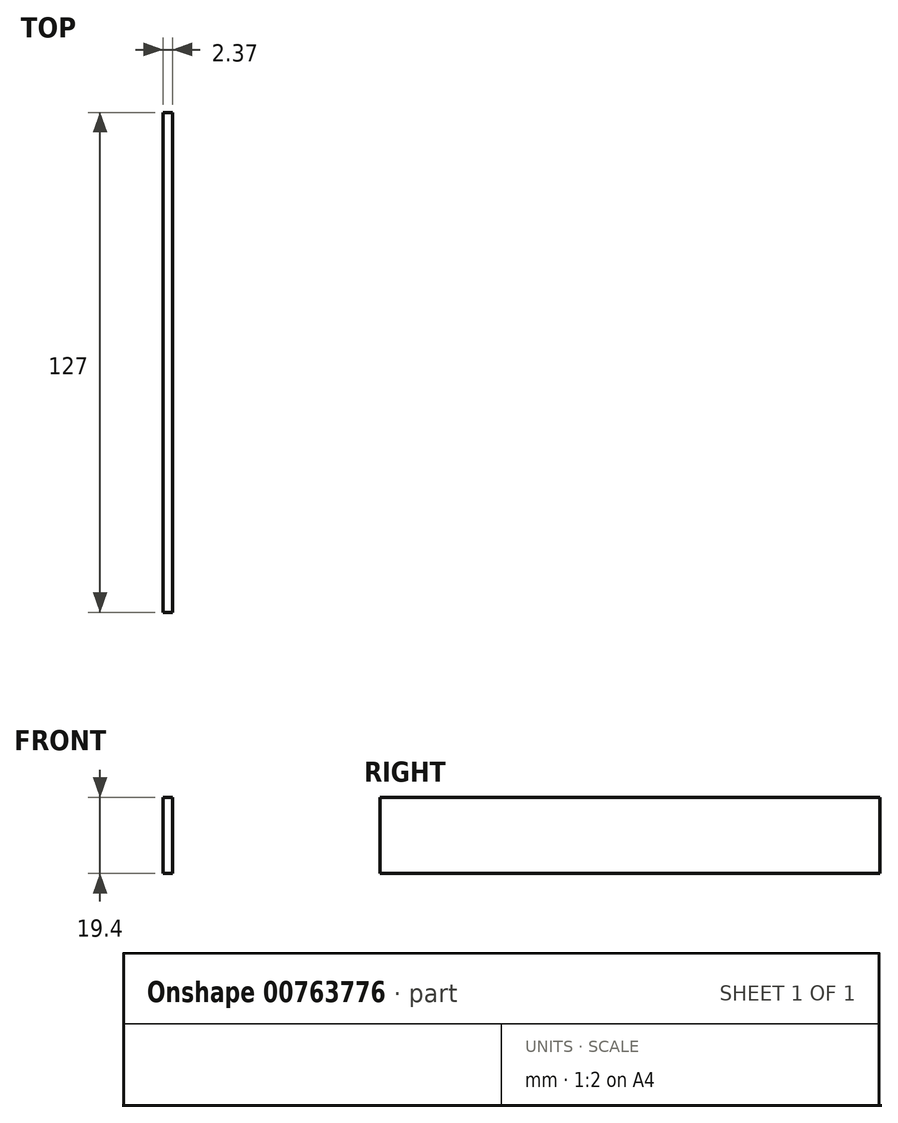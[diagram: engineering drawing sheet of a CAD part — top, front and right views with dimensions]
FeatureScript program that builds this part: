
annotation { "Feature Type Name" : "Feature", "Feature Type Description" : "" }
export const myFeature = defineFeature(function(context is Context, id is Id, definition is map)
    precondition{}
    {
        {
            var Q0;
            Q0=qCreatedBy(makeId("Front.planeOp"),FACE);
            var sketch = newSketch(context, id + "F0", { "sketchPlane" : qUnion([Q0])});
            skLineSegment(sketch, "E0.bottom", {"start": v(-47.21, 76.4) * mm, "end": v(-49.58, 76.4) * mm});
            skLineSegment(sketch, "E0.top", {"start": v(-47.21, 57) * mm, "end": v(-49.58, 57) * mm});
            skLineSegment(sketch, "E0.left", {"start": v(-47.21, 76.4) * mm, "end": v(-47.21, 57) * mm});
            skLineSegment(sketch, "E0.right", {"start": v(-49.58, 76.4) * mm, "end": v(-49.58, 57) * mm});
            skSolve(sketch);
        }
        {
            var Q0;
            Q0 = qSketchRegion(id + "F0", true);
            extrude(context, id + "F1", {"entities" : qUnion([Q0]), "depth" : 127 * mm, "offsetDistance" : 25.4 * mm});
        }
    });
